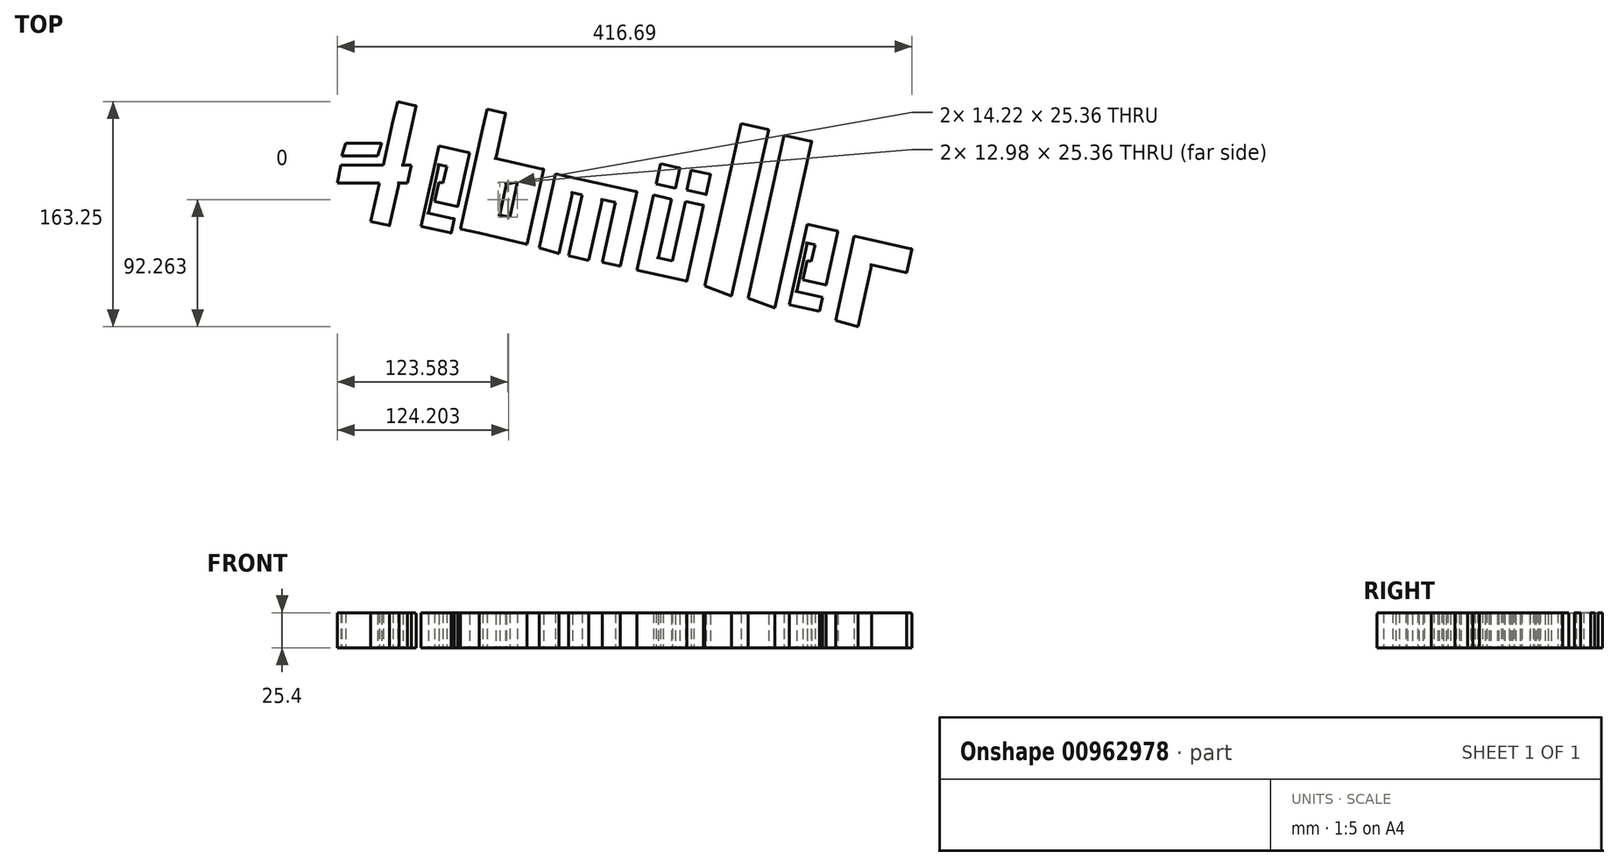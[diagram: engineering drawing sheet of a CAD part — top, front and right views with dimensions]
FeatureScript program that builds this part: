
annotation { "Feature Type Name" : "Feature", "Feature Type Description" : "" }
export const myFeature = defineFeature(function(context is Context, id is Id, definition is map)
    precondition{}
    {
        {
            var Q0;
            Q0=qCreatedBy(makeId("Top.planeOp"),FACE);
            var sketch = newSketch(context, id + "F0", { "sketchPlane" : qUnion([Q0])});
            skLineSegment(sketch, "E0", {"start": v(-95.9, 32.72) * mm, "end": v(-69.85, 32.72) * mm});
            skLineSegment(sketch, "E1", {"start": v(-69.85, 32.72) * mm, "end": v(-72.73, 23.28) * mm});
            skLineSegment(sketch, "E2", {"start": v(-72.73, 23.28) * mm, "end": v(-98.99, 23.28) * mm});
            skLineSegment(sketch, "E3", {"start": v(-98.99, 23.28) * mm, "end": v(-95.9, 32.72) * mm});
            skLineSegment(sketch, "E4", {"start": v(-61.65, 49.13) * mm, "end": v(-77.86, -24.1) * mm});
            skLineSegment(sketch, "E5", {"start": v(-77.86, -24.1) * mm, "end": v(-64.21, -27.13) * mm});
            skLineSegment(sketch, "E6", {"start": v(-64.21, -27.13) * mm, "end": v(-44.99, 59.75) * mm});
            skLineSegment(sketch, "E7", {"start": v(-44.99, 59.75) * mm, "end": v(-58.4, 62.72) * mm});
            skLineSegment(sketch, "E8", {"start": v(-58.4, 62.72) * mm, "end": v(-61.65, 49.13) * mm});
            skLineSegment(sketch, "E9", {"start": v(-41.36, 48.61) * mm, "end": v(-57.57, -24.63) * mm});
            skLineSegment(sketch, "E10", {"start": v(-57.57, -24.63) * mm, "end": v(-43.92, -27.65) * mm});
            skLineSegment(sketch, "E11", {"start": v(-43.92, -27.65) * mm, "end": v(-24.7, 59.23) * mm});
            skLineSegment(sketch, "E12", {"start": v(-24.7, 59.23) * mm, "end": v(-38.12, 62.2) * mm});
            skLineSegment(sketch, "E13", {"start": v(-38.12, 62.2) * mm, "end": v(-41.36, 48.61) * mm});
            skLineSegment(sketch, "E14", {"start": v(-99.38, 16.63) * mm, "end": v(-48.44, 16.63) * mm});
            skLineSegment(sketch, "E15", {"start": v(-48.44, 16.63) * mm, "end": v(-51.32, 3.62) * mm});
            skLineSegment(sketch, "E16", {"start": v(-51.32, 3.62) * mm, "end": v(-102.14, 3.62) * mm});
            skLineSegment(sketch, "E17", {"start": v(-102.14, 3.62) * mm, "end": v(-99.38, 16.63) * mm});
            skLineSegment(sketch, "E18", {"start": v(-22.79, 15.8) * mm, "end": v(-25.48, 3.62) * mm});
            skPoint(sketch, "E18.startSnap0", {"position": v(-34.31, 15.8) * mm});
            skLineSegment(sketch, "E19", {"start": v(-25.48, 3.62) * mm, "end": v(-28.37, 4.26) * mm});
            skLineSegment(sketch, "E20", {"start": v(-28.37, 4.26) * mm, "end": v(-31.44, -9.62) * mm});
            skLineSegment(sketch, "E21", {"start": v(-31.44, -9.62) * mm, "end": v(-14.8, -13.3) * mm});
            skLineSegment(sketch, "E22", {"start": v(-14.8, -13.3) * mm, "end": v(-6.18, 25.63) * mm});
            skLineSegment(sketch, "E23", {"start": v(-6.18, 25.63) * mm, "end": v(-28.5, 30.58) * mm});
            skLineSegment(sketch, "E24", {"start": v(-28.5, 30.58) * mm, "end": v(-41.39, -27.65) * mm});
            skLineSegment(sketch, "E25", {"start": v(-41.39, -27.65) * mm, "end": v(-19.48, -32.5) * mm});
            skLineSegment(sketch, "E26", {"start": v(-19.48, -32.5) * mm, "end": v(-17.22, -22.25) * mm});
            skLineSegment(sketch, "E27", {"start": v(-17.22, -22.25) * mm, "end": v(-35.95, -18.1) * mm});
            skLineSegment(sketch, "E28", {"start": v(-35.95, -18.1) * mm, "end": v(-28.37, 17.16) * mm});
            skLineSegment(sketch, "E29", {"start": v(-28.37, 17.16) * mm, "end": v(-22.79, 15.8) * mm});
            skLineSegment(sketch, "E30", {"start": v(3.33, 43.63) * mm, "end": v(-12.88, -29.61) * mm});
            skLineSegment(sketch, "E31", {"start": v(-12.88, -29.61) * mm, "end": v(0.76, -32.63) * mm});
            skLineSegment(sketch, "E32", {"start": v(0.76, -32.63) * mm, "end": v(19.99, 54.24) * mm});
            skLineSegment(sketch, "E33", {"start": v(19.99, 54.24) * mm, "end": v(6.57, 57.21) * mm});
            skLineSegment(sketch, "E34", {"start": v(6.57, 57.21) * mm, "end": v(3.33, 43.63) * mm});
            skLineSegment(sketch, "E35", {"start": v(12.72, 21.39) * mm, "end": v(34.01, 16.68) * mm});
            skLineSegment(sketch, "E36", {"start": v(34.01, 16.68) * mm, "end": v(47.55, 13.68) * mm});
            skLineSegment(sketch, "E37", {"start": v(47.55, 13.68) * mm, "end": v(35.49, -40.82) * mm});
            skLineSegment(sketch, "E38", {"start": v(35.49, -40.82) * mm, "end": v(0.76, -32.63) * mm});
            skLineSegment(sketch, "E39", {"start": v(20.53, 3.1) * mm, "end": v(15.57, -19.32) * mm});
            skLineSegment(sketch, "E40", {"start": v(15.57, -19.32) * mm, "end": v(22.94, -20.95) * mm});
            skLineSegment(sketch, "E41", {"start": v(22.94, -20.95) * mm, "end": v(28.55, 4.41) * mm});
            skLineSegment(sketch, "E42", {"start": v(28.55, 4.41) * mm, "end": v(20.53, 3.1) * mm});
            skLineSegment(sketch, "E43", {"start": v(44.3, -43.22) * mm, "end": v(56.18, 10.48) * mm});
            skLineSegment(sketch, "E44", {"start": v(56.18, 10.48) * mm, "end": v(115.11, -2.56) * mm});
            skLineSegment(sketch, "E45", {"start": v(115.11, -2.56) * mm, "end": v(103.16, -56.58) * mm});
            skLineSegment(sketch, "E46", {"start": v(103.16, -56.58) * mm, "end": v(89.99, -53.66) * mm});
            skLineSegment(sketch, "E47", {"start": v(89.99, -53.66) * mm, "end": v(99.57, -10.37) * mm});
            skLineSegment(sketch, "E48", {"start": v(99.57, -10.37) * mm, "end": v(90, -8.25) * mm});
            skLineSegment(sketch, "E49", {"start": v(90, -8.25) * mm, "end": v(80.24, -52.35) * mm});
            skLineSegment(sketch, "E50", {"start": v(80.24, -52.35) * mm, "end": v(65.65, -49.12) * mm});
            skLineSegment(sketch, "E51", {"start": v(65.65, -49.12) * mm, "end": v(75.46, -4.79) * mm});
            skLineSegment(sketch, "E52", {"start": v(75.46, -4.79) * mm, "end": v(68.46, -3.24) * mm});
            skLineSegment(sketch, "E53", {"start": v(68.46, -3.24) * mm, "end": v(58.67, -47.47) * mm});
            skLineSegment(sketch, "E54", {"start": v(58.67, -47.47) * mm, "end": v(44.3, -43.22) * mm});
            skLineSegment(sketch, "E55", {"start": v(127.18, -4.79) * mm, "end": v(115.07, -59.5) * mm});
            skLineSegment(sketch, "E56", {"start": v(115.07, -59.5) * mm, "end": v(151.24, -67.5) * mm});
            skLineSegment(sketch, "E57", {"start": v(151.24, -67.5) * mm, "end": v(163.43, -12.4) * mm});
            skLineSegment(sketch, "E58", {"start": v(163.43, -12.4) * mm, "end": v(150.38, -9.5) * mm});
            skLineSegment(sketch, "E59", {"start": v(150.38, -9.5) * mm, "end": v(140.8, -52.84) * mm});
            skLineSegment(sketch, "E60", {"start": v(140.8, -52.84) * mm, "end": v(130.73, -50.61) * mm});
            skLineSegment(sketch, "E61", {"start": v(130.73, -50.61) * mm, "end": v(140.14, -8.13) * mm});
            skLineSegment(sketch, "E62", {"start": v(140.14, -8.13) * mm, "end": v(127.18, -4.79) * mm});
            skLineSegment(sketch, "E63", {"start": v(129.03, 3.1) * mm, "end": v(143.05, 0) * mm});
            skLineSegment(sketch, "E64", {"start": v(143.05, 0) * mm, "end": v(146.28, 14.58) * mm});
            skLineSegment(sketch, "E65", {"start": v(146.28, 14.58) * mm, "end": v(134.08, 17.28) * mm});
            skLineSegment(sketch, "E66", {"start": v(129.03, 3.1) * mm, "end": v(132.27, 17.74) * mm});
            skLineSegment(sketch, "E67", {"start": v(132.27, 17.74) * mm, "end": v(134.08, 17.28) * mm});
            skLineSegment(sketch, "E68", {"start": v(151.3, -1.47) * mm, "end": v(165.32, -4.58) * mm});
            skLineSegment(sketch, "E69", {"start": v(165.32, -4.58) * mm, "end": v(168.55, 10) * mm});
            skLineSegment(sketch, "E70", {"start": v(168.55, 10) * mm, "end": v(156.35, 12.7) * mm});
            skLineSegment(sketch, "E71", {"start": v(151.3, -1.47) * mm, "end": v(154.54, 13.17) * mm});
            skLineSegment(sketch, "E72", {"start": v(154.54, 13.17) * mm, "end": v(156.35, 12.7) * mm});
            skLineSegment(sketch, "E73", {"start": v(164.42, -71.08) * mm, "end": v(190.53, 46.92) * mm});
            skLineSegment(sketch, "E74", {"start": v(190.53, 46.92) * mm, "end": v(210.52, 42.5) * mm});
            skLineSegment(sketch, "E75", {"start": v(210.52, 42.5) * mm, "end": v(183.79, -78.34) * mm});
            skLineSegment(sketch, "E76", {"start": v(183.79, -78.34) * mm, "end": v(164.42, -71.08) * mm});
            skLineSegment(sketch, "E77", {"start": v(195.79, -79.7) * mm, "end": v(221.9, 38.3) * mm});
            skLineSegment(sketch, "E78", {"start": v(221.9, 38.3) * mm, "end": v(241.9, 33.88) * mm});
            skLineSegment(sketch, "E79", {"start": v(241.9, 33.88) * mm, "end": v(215.15, -86.95) * mm});
            skLineSegment(sketch, "E80", {"start": v(215.15, -86.95) * mm, "end": v(195.79, -79.7) * mm});
            skLineSegment(sketch, "E81", {"start": v(244.19, -41.08) * mm, "end": v(241.5, -53.26) * mm});
            skLineSegment(sketch, "E82", {"start": v(241.5, -53.26) * mm, "end": v(238.6, -52.62) * mm});
            skLineSegment(sketch, "E83", {"start": v(238.6, -52.62) * mm, "end": v(235.53, -66.5) * mm});
            skLineSegment(sketch, "E84", {"start": v(235.53, -66.5) * mm, "end": v(252.18, -70.18) * mm});
            skLineSegment(sketch, "E85", {"start": v(252.18, -70.18) * mm, "end": v(260.8, -31.24) * mm});
            skLineSegment(sketch, "E86", {"start": v(260.8, -31.24) * mm, "end": v(238.47, -26.3) * mm});
            skLineSegment(sketch, "E87", {"start": v(238.47, -26.3) * mm, "end": v(225.58, -84.52) * mm});
            skLineSegment(sketch, "E88", {"start": v(225.58, -84.52) * mm, "end": v(247.49, -89.37) * mm});
            skLineSegment(sketch, "E89", {"start": v(247.49, -89.37) * mm, "end": v(249.76, -79.13) * mm});
            skLineSegment(sketch, "E90", {"start": v(249.76, -79.13) * mm, "end": v(231.02, -74.98) * mm});
            skLineSegment(sketch, "E91", {"start": v(231.02, -74.98) * mm, "end": v(238.6, -39.71) * mm});
            skLineSegment(sketch, "E92", {"start": v(238.6, -39.71) * mm, "end": v(244.19, -41.08) * mm});
            skLineSegment(sketch, "E93", {"start": v(259.19, -95.9) * mm, "end": v(272.7, -34.87) * mm});
            skLineSegment(sketch, "E94", {"start": v(272.7, -34.87) * mm, "end": v(314.55, -44.13) * mm});
            skLineSegment(sketch, "E95", {"start": v(314.55, -44.13) * mm, "end": v(310.74, -61.37) * mm});
            skLineSegment(sketch, "E96", {"start": v(310.74, -61.37) * mm, "end": v(285.3, -55.75) * mm});
            skLineSegment(sketch, "E97", {"start": v(285.3, -55.75) * mm, "end": v(275.39, -100.53) * mm});
            skLineSegment(sketch, "E98", {"start": v(275.39, -100.53) * mm, "end": v(259.19, -95.9) * mm});
            skSolve(sketch);
        }
        {
            var Q0;
            Q0=makeQuery(id+"F0.imprint","IMPRINT",FACE,{"disambiguationData":[TD([[makeQuery(id+"F0.imprint","IMPRINT",EDGE,{"derivedFrom":sQuery(id+"F0.wireOp",EDGE,"E0")}),-1.0]])]});
            var Q1;
            {var subQ5=sQuery(id+"F0.wireOp",EDGE,"E17");Q1=makeQuery(id+"F0.imprint","IMPRINT",FACE,{"disambiguationData":[TD([[makeQuery(id+"F0.imprint","IMPRINT",EDGE,{"derivedFrom":subQ5}),-1.0]])]});}
            var Q2;
            {var subQ0=sQuery(id+"F0.wireOp",EDGE,"E16");var subQ1=sQuery(id+"F0.wireOp",EDGE,"E4");var subQ2=makeQuery(id+"F0.imprint","INTERSECT",VERTEX,{"derivedFrom":[subQ1,subQ0]});Q2=makeQuery(id+"F0.imprint","IMPRINT",FACE,{"disambiguationData":[TD([[makeQuery(id+"F0.imprint","IMPRINT",EDGE,{"disambiguationData":[TD([[subQ2,1.0]])],"derivedFrom":subQ1}),1.0]])]});}
            var Q3;
            {var subQ0=sQuery(id+"F0.wireOp",EDGE,"E14");var subQ1=sQuery(id+"F0.wireOp",EDGE,"E6");var subQ2=makeQuery(id+"F0.imprint","INTERSECT",VERTEX,{"derivedFrom":[subQ1,subQ0]});Q3=makeQuery(id+"F0.imprint","IMPRINT",FACE,{"disambiguationData":[TD([[makeQuery(id+"F0.imprint","IMPRINT",EDGE,{"disambiguationData":[TD([[subQ2,1.0]])],"derivedFrom":subQ1}),-1.0]])]});}
            var Q4;
            {var subQ3=sQuery(id+"F0.wireOp",EDGE,"E5");Q4=makeQuery(id+"F0.imprint","IMPRINT",FACE,{"disambiguationData":[TD([[makeQuery(id+"F0.imprint","IMPRINT",EDGE,{"derivedFrom":subQ3}),1.0]])]});}
            var Q5;
            {var subQ0=sQuery(id+"F0.wireOp",EDGE,"E10");Q5=makeQuery(id+"F0.imprint","IMPRINT",FACE,{"disambiguationData":[TD([[makeQuery(id+"F0.imprint","IMPRINT",EDGE,{"derivedFrom":subQ0}),1.0]])]});}
            var Q6;
            Q6=makeQuery(id+"F0.imprint","IMPRINT",FACE,{"disambiguationData":[TD([[makeQuery(id+"F0.imprint","IMPRINT",EDGE,{"derivedFrom":sQuery(id+"F0.wireOp",EDGE,"E18")}),1.0]])]});
            var Q7;
            Q7=makeQuery(id+"F0.imprint","IMPRINT",FACE,{"disambiguationData":[TD([[makeQuery(id+"F0.imprint","IMPRINT",EDGE,{"derivedFrom":sQuery(id+"F0.wireOp",EDGE,"E30")}),1.0]])]});
            var Q8;
            {var subQ0=sQuery(id+"F0.wireOp",EDGE,"E35");Q8=makeQuery(id+"F0.imprint","IMPRINT",FACE,{"disambiguationData":[TD([[makeQuery(id+"F0.imprint","IMPRINT",EDGE,{"derivedFrom":subQ0}),-1.0]])]});}
            var Q9;
            Q9=makeQuery(id+"F0.imprint","IMPRINT",FACE,{"disambiguationData":[TD([[makeQuery(id+"F0.imprint","IMPRINT",EDGE,{"derivedFrom":sQuery(id+"F0.wireOp",EDGE,"E43")}),-1.0]])]});
            var Q10;
            Q10=makeQuery(id+"F0.imprint","IMPRINT",FACE,{"disambiguationData":[TD([[makeQuery(id+"F0.imprint","IMPRINT",EDGE,{"derivedFrom":sQuery(id+"F0.wireOp",EDGE,"E55")}),1.0]])]});
            var Q11;
            Q11=makeQuery(id+"F0.imprint","IMPRINT",FACE,{"disambiguationData":[TD([[makeQuery(id+"F0.imprint","IMPRINT",EDGE,{"derivedFrom":sQuery(id+"F0.wireOp",EDGE,"E68")}),1.0]])]});
            var Q12;
            Q12=makeQuery(id+"F0.imprint","IMPRINT",FACE,{"disambiguationData":[TD([[makeQuery(id+"F0.imprint","IMPRINT",EDGE,{"derivedFrom":sQuery(id+"F0.wireOp",EDGE,"E63")}),1.0]])]});
            var Q13;
            Q13=makeQuery(id+"F0.imprint","IMPRINT",FACE,{"disambiguationData":[TD([[makeQuery(id+"F0.imprint","IMPRINT",EDGE,{"derivedFrom":sQuery(id+"F0.wireOp",EDGE,"E73")}),-1.0]])]});
            var Q14;
            Q14=makeQuery(id+"F0.imprint","IMPRINT",FACE,{"disambiguationData":[TD([[makeQuery(id+"F0.imprint","IMPRINT",EDGE,{"derivedFrom":sQuery(id+"F0.wireOp",EDGE,"E77")}),-1.0]])]});
            var Q15;
            Q15=makeQuery(id+"F0.imprint","IMPRINT",FACE,{"disambiguationData":[TD([[makeQuery(id+"F0.imprint","IMPRINT",EDGE,{"derivedFrom":sQuery(id+"F0.wireOp",EDGE,"E81")}),1.0]])]});
            var Q16;
            Q16=makeQuery(id+"F0.imprint","IMPRINT",FACE,{"disambiguationData":[TD([[makeQuery(id+"F0.imprint","IMPRINT",EDGE,{"derivedFrom":sQuery(id+"F0.wireOp",EDGE,"E93")}),-1.0]])]});
            var Q17;
            {var subQ1=sQuery(id+"F0.wireOp",EDGE,"E7");Q17=makeQuery(id+"F0.imprint","IMPRINT",FACE,{"disambiguationData":[TD([[makeQuery(id+"F0.imprint","IMPRINT",EDGE,{"derivedFrom":subQ1}),1.0]])]});}
            extrude(context, id + "F1", {"entities" : qUnion([Q0, Q1, Q2, Q3, Q4, Q5, Q6, Q7, Q8, Q9, Q10, Q11, Q12, Q13, Q14, Q15, Q16, Q17]), "depth" : 25.4 * mm, "offsetDistance" : 25.4 * mm});
        }
        {
            var Q0;
            {var subQ0=sQuery(id+"F0.wireOp",EDGE,"E6");Q0=makeQuery(id+"F1.opExtrude","CAP_EDGE",EDGE,{"disambiguationData":[OSD([subQ0]),TDD([makeQuery(id+"F0.imprint","IMPRINT",EDGE,{"disambiguationData":[TD([[makeQuery(id+"F0.imprint","INTERSECT",VERTEX,{"derivedFrom":[subQ0,sQuery(id+"F0.wireOp",EDGE,"E14")]}),-1.0]])],"derivedFrom":subQ0})])],"isStart":false});}
            var Q1;
            {var subQ0=sQuery(id+"F0.wireOp",EDGE,"E6");Q1=makeQuery(id+"F1.opExtrude","CAP_EDGE",EDGE,{"disambiguationData":[OSD([subQ0]),TDD([makeQuery(id+"F0.imprint","IMPRINT",EDGE,{"disambiguationData":[TD([[makeQuery(id+"F0.imprint","INTERSECT",VERTEX,{"derivedFrom":[sQuery(id+"F0.wireOp",EDGE,"E5"),subQ0]}),-1.0]])],"derivedFrom":subQ0})])],"isStart":false});}
            var Q2;
            Q2=makeQuery(id+"F1.opExtrude","CAP_EDGE",EDGE,{"disambiguationData":[OSD([sQuery(id+"F0.wireOp",EDGE,"E11")])],"isStart":false});
            var Q3;
            Q3=makeQuery(id+"F1.opExtrude","CAP_EDGE",EDGE,{"disambiguationData":[OSD([sQuery(id+"F0.wireOp",EDGE,"E28")])],"isStart":false});
            var Q4;
            Q4=makeQuery(id+"F1.opExtrude","CAP_EDGE",EDGE,{"disambiguationData":[OSD([sQuery(id+"F0.wireOp",EDGE,"E1")])],"isStart":false});
            var Q5;
            Q5=makeQuery(id+"F1.opExtrude","CAP_EDGE",EDGE,{"disambiguationData":[OSD([sQuery(id+"F0.wireOp",EDGE,"E22")])],"isStart":false});
            var Q6;
            Q6=makeQuery(id+"F1.opExtrude","CAP_EDGE",EDGE,{"disambiguationData":[OSD([sQuery(id+"F0.wireOp",EDGE,"E26")])],"isStart":false});
            var Q7;
            Q7=makeQuery(id+"F1.opExtrude","CAP_EDGE",EDGE,{"disambiguationData":[OSD([sQuery(id+"F0.wireOp",EDGE,"E32")])],"isStart":false});
            var Q8;
            Q8=makeQuery(id+"F1.opExtrude","CAP_EDGE",EDGE,{"disambiguationData":[OSD([sQuery(id+"F0.wireOp",EDGE,"E39")])],"isStart":false});
            var Q9;
            Q9=makeQuery(id+"F1.opExtrude","CAP_EDGE",EDGE,{"disambiguationData":[OSD([sQuery(id+"F0.wireOp",EDGE,"E37")])],"isStart":false});
            var Q10;
            Q10=makeQuery(id+"F1.opExtrude","CAP_EDGE",EDGE,{"disambiguationData":[OSD([sQuery(id+"F0.wireOp",EDGE,"E53")])],"isStart":false});
            var Q11;
            Q11=makeQuery(id+"F1.opExtrude","CAP_EDGE",EDGE,{"disambiguationData":[OSD([sQuery(id+"F0.wireOp",EDGE,"E49")])],"isStart":false});
            var Q12;
            Q12=makeQuery(id+"F1.opExtrude","CAP_EDGE",EDGE,{"disambiguationData":[OSD([sQuery(id+"F0.wireOp",EDGE,"E45")])],"isStart":false});
            var Q13;
            Q13=makeQuery(id+"F1.opExtrude","CAP_EDGE",EDGE,{"disambiguationData":[OSD([sQuery(id+"F0.wireOp",EDGE,"E61")])],"isStart":false});
            var Q14;
            Q14=makeQuery(id+"F1.opExtrude","CAP_EDGE",EDGE,{"disambiguationData":[OSD([sQuery(id+"F0.wireOp",EDGE,"E57")])],"isStart":false});
            var Q15;
            Q15=makeQuery(id+"F1.opExtrude","CAP_EDGE",EDGE,{"disambiguationData":[OSD([sQuery(id+"F0.wireOp",EDGE,"E75")])],"isStart":false});
            var Q16;
            Q16=makeQuery(id+"F1.opExtrude","CAP_EDGE",EDGE,{"disambiguationData":[OSD([sQuery(id+"F0.wireOp",EDGE,"E79")])],"isStart":false});
            var Q17;
            Q17=makeQuery(id+"F1.opExtrude","CAP_EDGE",EDGE,{"disambiguationData":[OSD([sQuery(id+"F0.wireOp",EDGE,"E91")])],"isStart":false});
            var Q18;
            Q18=makeQuery(id+"F1.opExtrude","CAP_EDGE",EDGE,{"disambiguationData":[OSD([sQuery(id+"F0.wireOp",EDGE,"E85")])],"isStart":false});
            var Q19;
            Q19=makeQuery(id+"F1.opExtrude","CAP_EDGE",EDGE,{"disambiguationData":[OSD([sQuery(id+"F0.wireOp",EDGE,"E97")])],"isStart":false});
            var Q20;
            Q20=makeQuery(id+"F1.opExtrude","CAP_EDGE",EDGE,{"disambiguationData":[OSD([sQuery(id+"F0.wireOp",EDGE,"E95")])],"isStart":false});
            var Q21;
            Q21=makeQuery(id+"F1.opExtrude","CAP_EDGE",EDGE,{"disambiguationData":[OSD([sQuery(id+"F0.wireOp",EDGE,"E64")])],"isStart":false});
            var Q22;
            Q22=makeQuery(id+"F1.opExtrude","CAP_EDGE",EDGE,{"disambiguationData":[OSD([sQuery(id+"F0.wireOp",EDGE,"E69")])],"isStart":false});
            fillet(context, id + "F2", {"entities" : qUnion([Q0, Q1, Q2, Q3, Q4, Q5, Q6, Q7, Q8, Q9, Q10, Q11, Q12, Q13, Q14, Q15, Q16, Q17, Q18, Q19, Q20, Q21, Q22]), "radius" : 1.27 * mm, "tangentPropagation" : true, "allowEdgeOverflow" : false});
        }
    });
